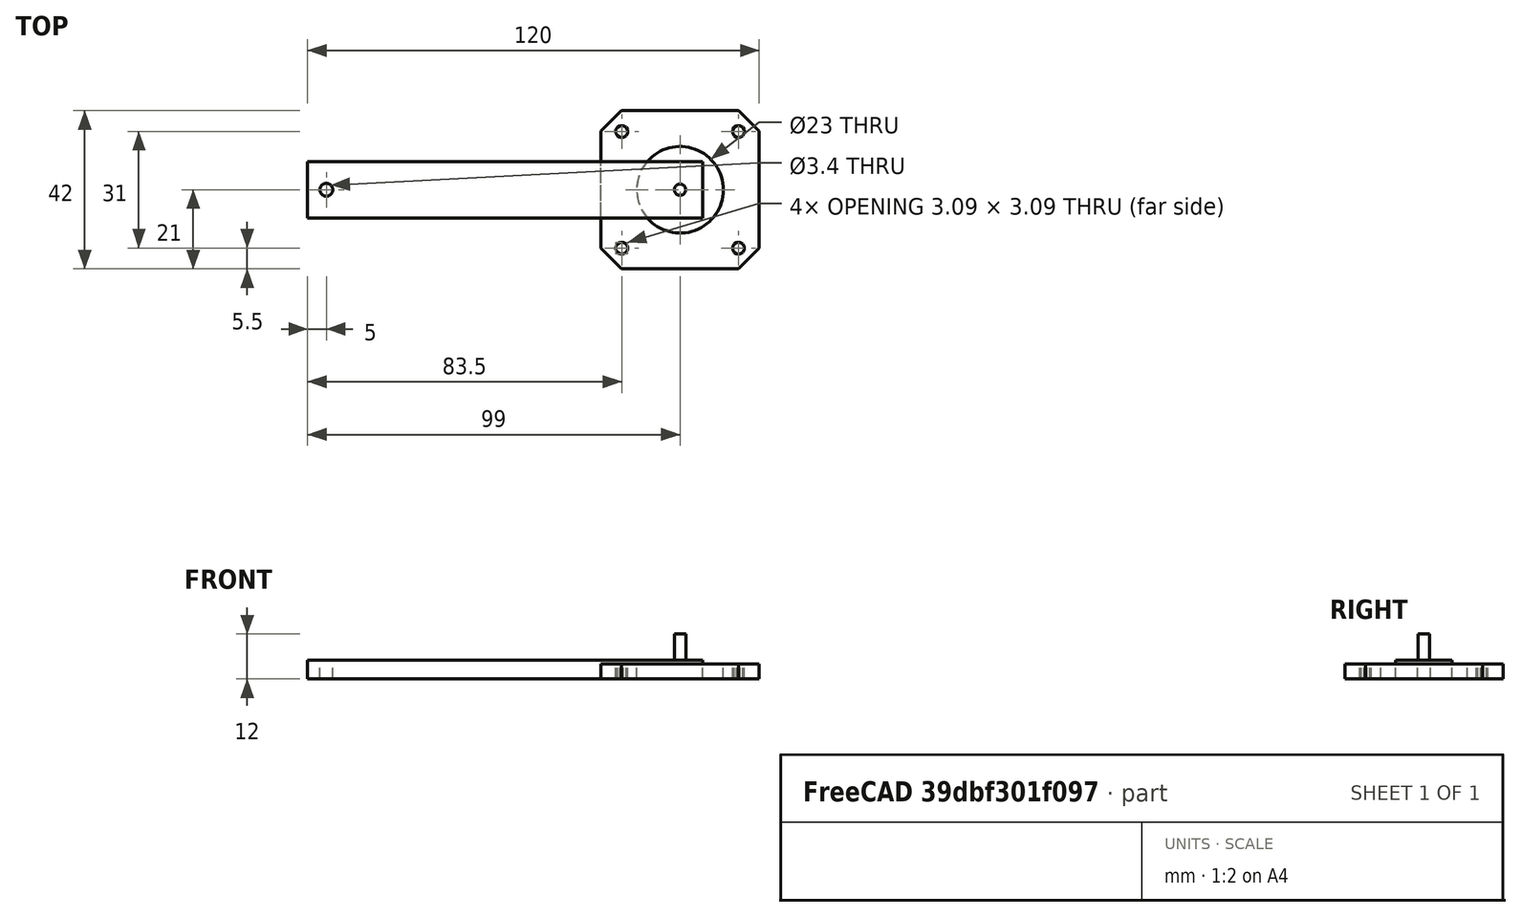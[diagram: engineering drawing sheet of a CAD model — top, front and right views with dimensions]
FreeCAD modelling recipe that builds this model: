
FCSTD DOCUMENT  (FreeCAD 0.14R3702 (Git))
Label: handdriven
License: CC-BY 3.0
LicenseURL: http://creativecommons.org/licenses/by/3.0/
objects: Part::Box×6, Part::Fuse×6, Part::Prism×4, Part::Cylinder×3, Part::Cut×2, Part::MultiFuse×1
note: 22 computed .brp shape members not serialized (recipe doc carries the construction recipe); baked Part::Feature solids carry a one-line shape summary decoded from their .brp

FEATURE [Part::Box] cube
  Height = 4
  Length = 42
  Placement = pos=(-21,-21,0) rot=(0,0,1;0rad)
  Width = 42
FEATURE [Part::Box] cube001
  Height = 4.2
  Length = 5
  Placement = pos=(25.8345,-5,-0.1) rot=(0,0,1;0rad)
  Width = 10
FEATURE [Part::Prism] prism
  Circumradius = 1.6
  Height = 16
  Placement = pos=(21.9203,0,-8) rot=(0,0,1;0rad)
  Polygon = 12
FEATURE [Part::Fuse] union
  Base = -> cube001
  Placement = pos=(0,0,0) rot=(0,0,1;0.785398rad)
  Tool = -> prism
FEATURE [Part::Box] cube002
  Height = 4.2
  Length = 5
  Placement = pos=(25.8345,-5,-0.1) rot=(0,0,1;0rad)
  Width = 10
FEATURE [Part::Prism] prism001
  Circumradius = 1.6
  Height = 16
  Placement = pos=(21.9203,0,-8) rot=(0,0,1;0rad)
  Polygon = 12
FEATURE [Part::Fuse] union001
  Base = -> cube002
  Placement = pos=(0,0,0) rot=(0,0,1;2.35619rad)
  Tool = -> prism001
FEATURE [Part::Box] cube003
  Height = 4.2
  Length = 5
  Placement = pos=(25.8345,-5,-0.1) rot=(0,0,1;0rad)
  Width = 10
FEATURE [Part::Prism] prism002
  Circumradius = 1.6
  Height = 16
  Placement = pos=(21.9203,0,-8) rot=(0,0,1;0rad)
  Polygon = 12
FEATURE [Part::Fuse] union002
  Base = -> cube003
  Placement = pos=(0,0,0) rot=(0,0,1;3.92699rad)
  Tool = -> prism002
FEATURE [Part::Box] cube004
  Height = 4.2
  Length = 5
  Placement = pos=(25.8345,-5,-0.1) rot=(0,0,1;0rad)
  Width = 10
FEATURE [Part::Prism] prism003
  Circumradius = 1.6
  Height = 16
  Placement = pos=(21.9203,0,-8) rot=(0,0,1;0rad)
  Polygon = 12
FEATURE [Part::Fuse] union003
  Base = -> cube004
  Placement = pos=(0,0,0) rot=(0,0,-1;0.785398rad)
  Tool = -> prism003
FEATURE [Part::MultiFuse] Group
  Shapes = -> [union,union001,union002,union003]
FEATURE [Part::Cylinder] cylinder
  Angle = 360
  Height = 8.8
  Placement = pos=(0,0,-4.4) rot=(0,0,1;0rad)
  Radius = 11.5
FEATURE [Part::Fuse] union004
  Base = -> Group
  Tool = -> cylinder
FEATURE [Part::Cut] difference
  Base = -> cube
  Tool = -> union004
FEATURE [Part::Box] Box  label="Cube"
  Height = 5
  Length = 105
  Placement = pos=(-99,-7.5,0) rot=(0,0,1;0rad)
  Width = 15
FEATURE [Part::Cylinder] Cylinder
  Angle = 360
  Height = 10
  Placement = pos=(-94,0,-4) rot=(0,0,1;0rad)
  Radius = 1.7
FEATURE [Part::Cut] Cut
  Base = -> Box
  Tool = -> Cylinder
FEATURE [Part::Cylinder] Cylinder001
  Angle = 360
  Height = 10
  Placement = pos=(0,0,2) rot=(0,0,1;0rad)
  Radius = 1.5
FEATURE [Part::Fuse] Fusion
  Base = -> Cut
  Tool = -> Cylinder001
